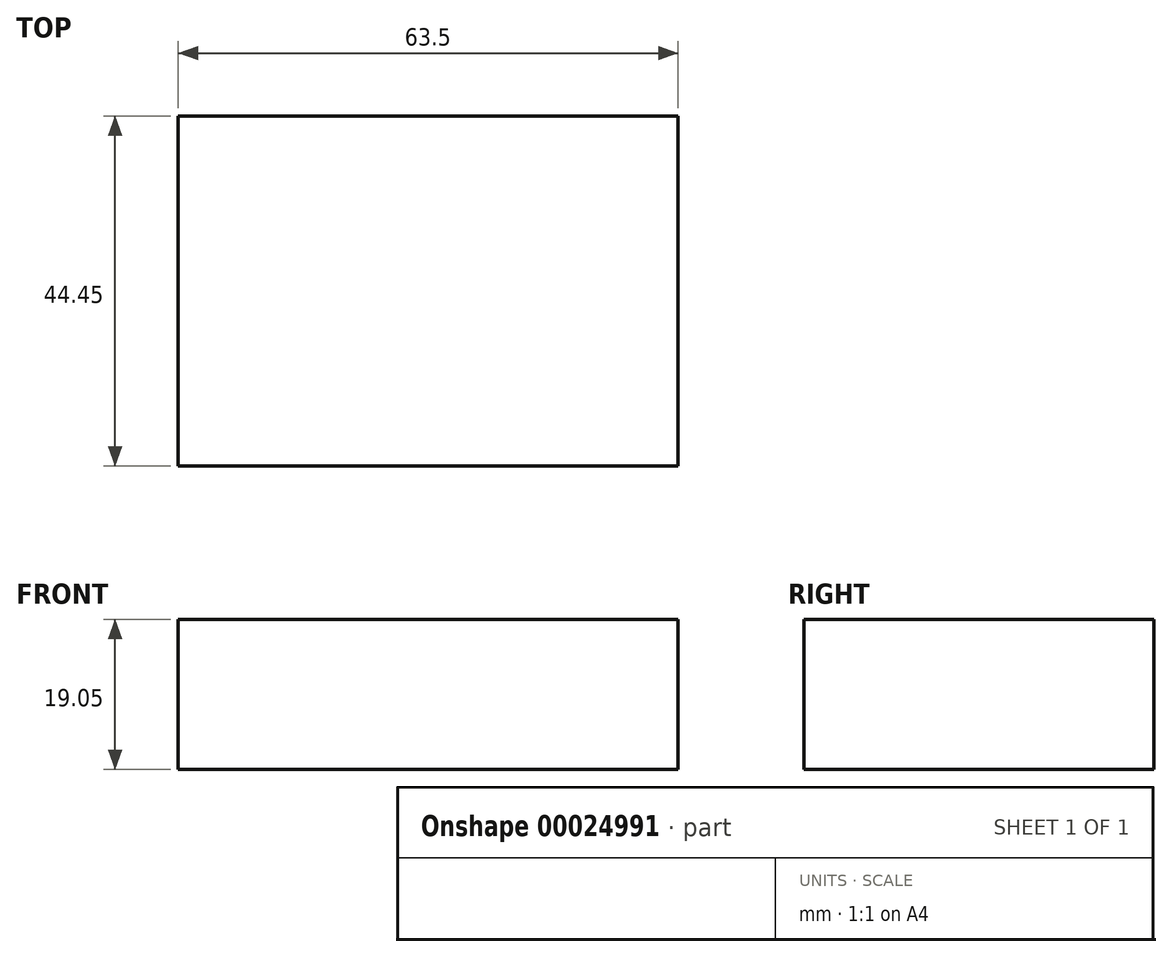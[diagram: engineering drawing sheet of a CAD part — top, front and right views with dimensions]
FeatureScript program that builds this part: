
annotation { "Feature Type Name" : "Feature", "Feature Type Description" : "" }
export const myFeature = defineFeature(function(context is Context, id is Id, definition is map)
    precondition{}
    {
        {
            var Q0;
            Q0=qCreatedBy(makeId("Front.planeOp"),FACE);
            var sketch = newSketch(context, id + "F0", { "sketchPlane" : qUnion([Q0])});
            skLineSegment(sketch, "E0.bottom", {"start": v(-40.45, 11.88) * mm, "end": v(23.05, 11.88) * mm});
            skLineSegment(sketch, "E0.top", {"start": v(-40.45, -7.17) * mm, "end": v(23.05, -7.17) * mm});
            skLineSegment(sketch, "E0.left", {"start": v(-40.45, 11.88) * mm, "end": v(-40.45, -7.17) * mm});
            skLineSegment(sketch, "E0.right", {"start": v(23.05, 11.88) * mm, "end": v(23.05, -7.17) * mm});
            skSolve(sketch);
        }
        {
            var Q0;
            Q0 = qSketchRegion(id + "F0", true);
            extrude(context, id + "F1", {"entities" : qUnion([Q0]), "depth" : 44.45 * mm});
        }
    });
